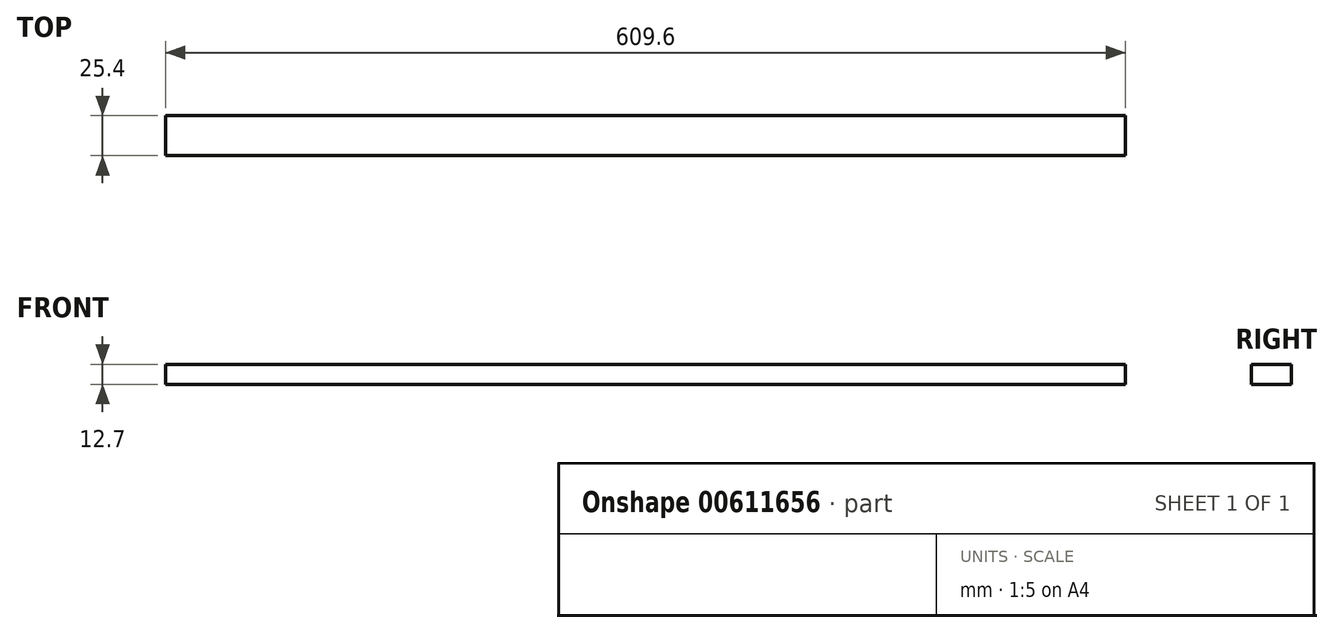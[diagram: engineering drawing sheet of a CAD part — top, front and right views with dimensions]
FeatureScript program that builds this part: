
annotation { "Feature Type Name" : "Feature", "Feature Type Description" : "" }
export const myFeature = defineFeature(function(context is Context, id is Id, definition is map)
    precondition{}
    {
        {
            var Q0;
            Q0=qCreatedBy(makeId("Right.planeOp"),FACE);
            var sketch = newSketch(context, id + "F0", { "sketchPlane" : qUnion([Q0])});
            skLineSegment(sketch, "E0", {"start": v(12.7, 6.35) * mm, "end": v(12.7, -6.35) * mm});
            skLineSegment(sketch, "E1", {"start": v(12.7, -6.35) * mm, "end": v(-12.7, -6.35) * mm});
            skLineSegment(sketch, "E2", {"start": v(-12.7, -6.35) * mm, "end": v(-12.7, 6.35) * mm});
            skLineSegment(sketch, "E3", {"start": v(-12.7, 6.35) * mm, "end": v(12.7, 6.35) * mm});
            skSolve(sketch);
        }
        {
            var Q0;
            Q0 = qSketchRegion(id + "F0", true);
            extrude(context, id + "F1", {"entities" : qUnion([Q0]), "depth" : 609.6 * mm, "offsetDistance" : 25.4 * mm});
        }
    });
